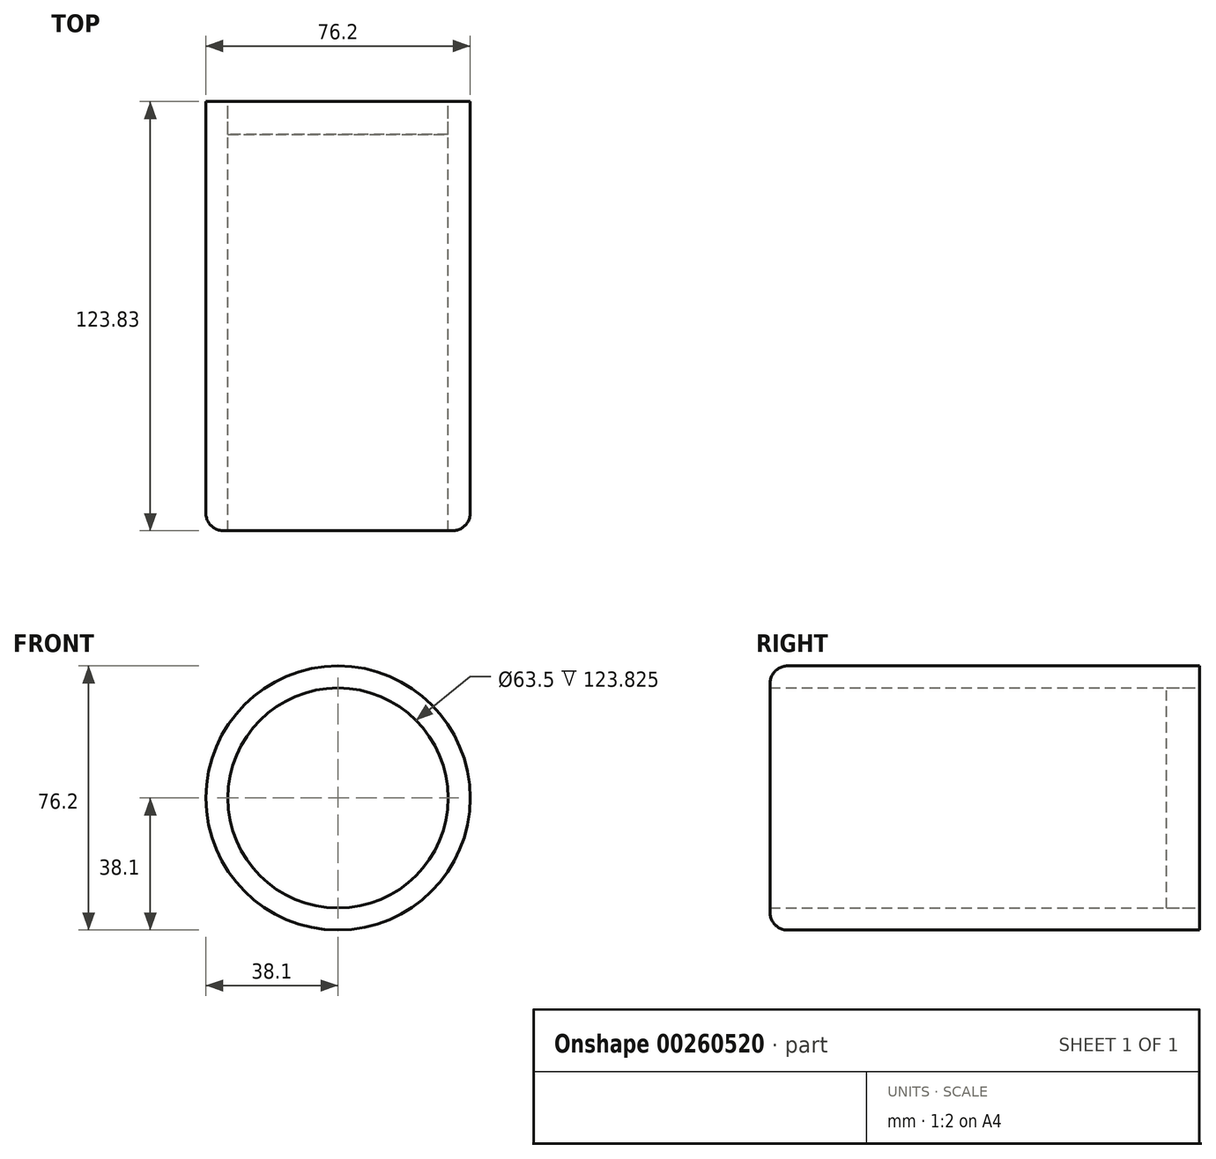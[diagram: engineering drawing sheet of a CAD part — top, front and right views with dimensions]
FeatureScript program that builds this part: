
annotation { "Feature Type Name" : "Feature", "Feature Type Description" : "" }
export const myFeature = defineFeature(function(context is Context, id is Id, definition is map)
    precondition{}
    {
        {
            var Q0;
            Q0=qCreatedBy(makeId("Front.planeOp"),FACE);
            var sketch = newSketch(context, id + "F0", { "sketchPlane" : qUnion([Q0])});
            skCircle(sketch, "E0", {"center": v(0, 0) * mm, "radius": 38.1 * mm});
            skCircle(sketch, "E1", {"center": v(0, 0) * mm, "radius": 31.75 * mm});
            skSolve(sketch);
        }
        {
            var Q0;
            Q0 = qSketchRegion(id + "F0", true);
            extrude(context, id + "F1", {"entities" : qUnion([Q0]), "depth" : 123.82 * mm});
        }
        {
            var Q0;
            Q0=makeQuery(id+"F0.imprint","IMPRINT",FACE,{"disambiguationData":[TD([[makeQuery(id+"F0.imprint","IMPRINT",EDGE,{"derivedFrom":sQuery(id+"F0.wireOp",EDGE,"E1")}),1.0]])]});
            extrude(context, id + "F2", {"entities" : qUnion([Q0]), "depth" : 9.52 * mm});
        }
        {
            var Q0;
            Q0=makeQuery(id+"F1.opExtrude","CAP_EDGE",EDGE,{"disambiguationData":[OSD([sQuery(id+"F0.wireOp",EDGE,"E0")])],"isStart":false});
            fillet(context, id + "F3", {"entities" : qUnion([Q0]), "radius" : 5.08 * mm, "tangentPropagation" : true, "allowEdgeOverflow" : false});
        }
    });
